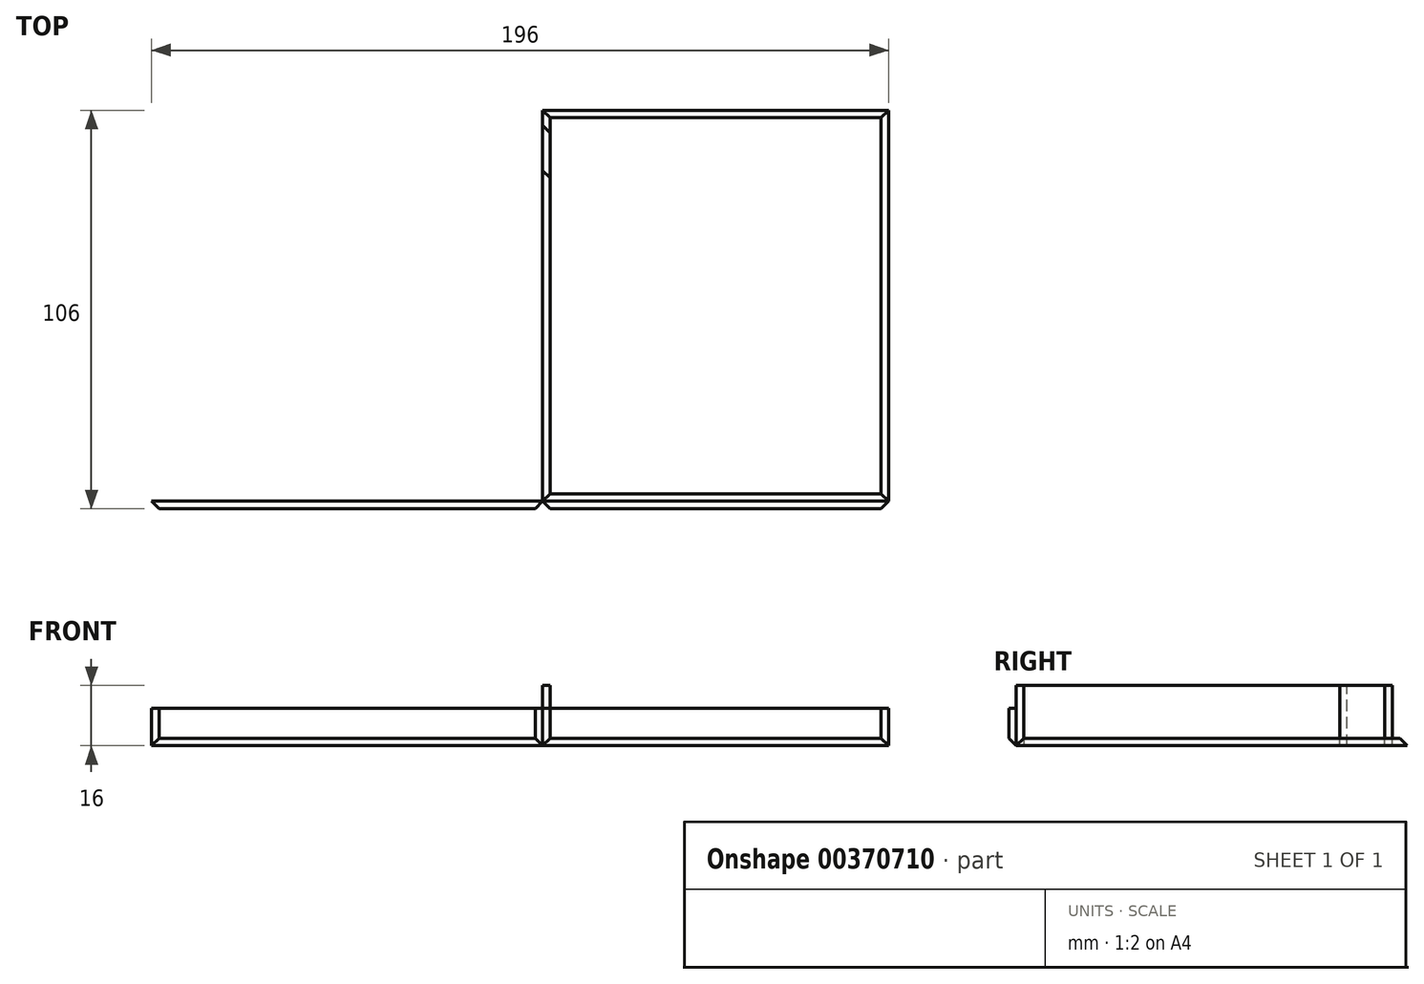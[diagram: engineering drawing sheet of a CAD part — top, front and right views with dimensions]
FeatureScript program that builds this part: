
annotation { "Feature Type Name" : "Feature", "Feature Type Description" : "" }
export const myFeature = defineFeature(function(context is Context, id is Id, definition is map)
    precondition{}
    {
        {
            var Q0;
            Q0=qCreatedBy(makeId("Top.planeOp"),FACE);
            var sketch = newSketch(context, id + "F0", { "sketchPlane" : qUnion([Q0])});
            skLineSegment(sketch, "E0.bottom", {"start": v(0, 0) * mm, "end": v(92, 0) * mm});
            skLineSegment(sketch, "E0.top", {"start": v(0, 104) * mm, "end": v(92, 104) * mm});
            skLineSegment(sketch, "E0.left", {"start": v(0, 0) * mm, "end": v(0, 104) * mm});
            skLineSegment(sketch, "E0.right", {"start": v(92, 0) * mm, "end": v(92, 104) * mm});
            skSolve(sketch);
        }
        {
            var Q0;
            Q0=makeQuery(id+"F0.imprint","IMPRINT",FACE,{"disambiguationData":[TD([[makeQuery(id+"F0.imprint","IMPRINT",EDGE,{"derivedFrom":sQuery(id+"F0.wireOp",EDGE,"E0.bottom")}),1.0]])]});
            extrude(context, id + "F1", {"entities" : qUnion([Q0]), "depth" : 2 * mm});
        }
        {
            var Q0;
            Q0=makeQuery(id+"F1.opExtrude","CAP_FACE",FACE,{"disambiguationData":[OSD([sQuery(id+"F0.wireOp",EDGE,"E0.bottom"),sQuery(id+"F0.wireOp",EDGE,"E0.top"),sQuery(id+"F0.wireOp",EDGE,"E0.left"),sQuery(id+"F0.wireOp",EDGE,"E0.right")])],"isStart":false});
            chamfer(context, id + "F2", {"entities" : qUnion([Q0]), "width" : 2 * mm, "tangentPropagation" : true});
        }
        {
            var Q0;
            Q0=qCreatedBy(makeId("Front.planeOp"),FACE);
            var sketch = newSketch(context, id + "F3", { "sketchPlane" : qUnion([Q0])});
            skLineSegment(sketch, "E1.bottom", {"start": v(0, 0) * mm, "end": v(-104, 0) * mm});
            skLineSegment(sketch, "E1.top", {"start": v(0, 10) * mm, "end": v(-104, 10) * mm});
            skLineSegment(sketch, "E1.left", {"start": v(0, 0) * mm, "end": v(0, 10) * mm});
            skLineSegment(sketch, "E1.right", {"start": v(-104, 0) * mm, "end": v(-104, 10) * mm});
            skSolve(sketch);
        }
        {
            var Q0;
            Q0=makeQuery(id+"F3.imprint","IMPRINT",FACE,{"disambiguationData":[TD([[makeQuery(id+"F3.imprint","IMPRINT",EDGE,{"derivedFrom":sQuery(id+"F3.wireOp",EDGE,"E1.bottom")}),-1.0]])]});
            extrude(context, id + "F4", {"entities" : qUnion([Q0]), "depth" : 2 * mm});
        }
        {
            var Q0;
            Q0=makeQuery(id+"F4.opExtrude","CAP_EDGE",EDGE,{"disambiguationData":[OSD([sQuery(id+"F3.wireOp",EDGE,"E1.bottom")])],"isStart":false});
            var Q1;
            Q1=makeQuery(id+"F4.opExtrude","CAP_EDGE",EDGE,{"disambiguationData":[OSD([sQuery(id+"F3.wireOp",EDGE,"E1.left")])],"isStart":false});
            var Q2;
            Q2=makeQuery(id+"F4.opExtrude","CAP_EDGE",EDGE,{"disambiguationData":[OSD([sQuery(id+"F3.wireOp",EDGE,"E1.right")])],"isStart":false});
            chamfer(context, id + "F5", {"entities" : qUnion([Q0, Q1, Q2]), "width" : 2 * mm, "tangentPropagation" : true});
        }
        {
            var Q0;
            Q0=qCreatedBy(makeId("Front.planeOp"),FACE);
            var sketch = newSketch(context, id + "F6", { "sketchPlane" : qUnion([Q0])});
            skLineSegment(sketch, "E2.bottom", {"start": v(0, 0) * mm, "end": v(92, 0) * mm});
            skLineSegment(sketch, "E2.top", {"start": v(0, 10) * mm, "end": v(92, 10) * mm});
            skLineSegment(sketch, "E2.left", {"start": v(0, 0) * mm, "end": v(0, 10) * mm});
            skLineSegment(sketch, "E2.right", {"start": v(92, 0) * mm, "end": v(92, 10) * mm});
            skSolve(sketch);
        }
        {
            var Q0;
            Q0=makeQuery(id+"F6.imprint","IMPRINT",FACE,{"disambiguationData":[TD([[makeQuery(id+"F6.imprint","IMPRINT",EDGE,{"derivedFrom":sQuery(id+"F6.wireOp",EDGE,"E2.bottom")}),1.0]])]});
            extrude(context, id + "F7", {"entities" : qUnion([Q0]), "depth" : 2 * mm});
        }
        {
            var Q0;
            Q0=makeQuery(id+"F7.opExtrude","CAP_EDGE",EDGE,{"disambiguationData":[OSD([sQuery(id+"F6.wireOp",EDGE,"E2.left")])],"isStart":false});
            var Q1;
            Q1=makeQuery(id+"F7.opExtrude","CAP_EDGE",EDGE,{"disambiguationData":[OSD([sQuery(id+"F6.wireOp",EDGE,"E2.bottom")])],"isStart":false});
            var Q2;
            Q2=makeQuery(id+"F7.opExtrude","CAP_EDGE",EDGE,{"disambiguationData":[OSD([sQuery(id+"F6.wireOp",EDGE,"E2.right")])],"isStart":false});
            chamfer(context, id + "F8", {"entities" : qUnion([Q0, Q1, Q2]), "width" : 2 * mm, "tangentPropagation" : true});
        }
        {
            var Q0;
            Q0=qCreatedBy(makeId("Right.planeOp"),FACE);
            var sketch = newSketch(context, id + "F9", { "sketchPlane" : qUnion([Q0])});
            skLineSegment(sketch, "E3.bottom", {"start": v(0, 0) * mm, "end": v(100, 0) * mm});
            skLineSegment(sketch, "E3.top", {"start": v(0, 16) * mm, "end": v(100, 16) * mm});
            skLineSegment(sketch, "E3.left", {"start": v(0, 0) * mm, "end": v(0, 16) * mm});
            skLineSegment(sketch, "E3.right", {"start": v(100, 0) * mm, "end": v(100, 16) * mm});
            skSolve(sketch);
        }
        {
            var Q0;
            Q0=makeQuery(id+"F9.imprint","IMPRINT",FACE,{"disambiguationData":[TD([[makeQuery(id+"F9.imprint","IMPRINT",EDGE,{"derivedFrom":sQuery(id+"F9.wireOp",EDGE,"E3.bottom")}),1.0]])]});
            extrude(context, id + "F10", {"entities" : qUnion([Q0]), "depth" : 2 * mm});
        }
        {
            var Q0;
            Q0=makeQuery(id+"F10.opExtrude","CAP_EDGE",EDGE,{"disambiguationData":[OSD([sQuery(id+"F9.wireOp",EDGE,"E3.right")])],"isStart":false});
            var Q1;
            Q1=makeQuery(id+"F10.opExtrude","CAP_EDGE",EDGE,{"disambiguationData":[OSD([sQuery(id+"F9.wireOp",EDGE,"E3.left")])],"isStart":false});
            chamfer(context, id + "F11", {"entities" : qUnion([Q0, Q1]), "width" : 2 * mm, "tangentPropagation" : true});
        }
        {
            var Q0;
            Q0=qCreatedBy(makeId("Right.planeOp"),FACE);
            var sketch = newSketch(context, id + "F12", { "sketchPlane" : qUnion([Q0])});
            skLineSegment(sketch, "E4.bottom", {"start": v(0, 0) * mm, "end": v(88, 0) * mm});
            skLineSegment(sketch, "E4.top", {"start": v(0, 16) * mm, "end": v(88, 16) * mm});
            skLineSegment(sketch, "E4.left", {"start": v(0, 0) * mm, "end": v(0, 16) * mm});
            skLineSegment(sketch, "E4.right", {"start": v(88, 0) * mm, "end": v(88, 16) * mm});
            skSolve(sketch);
        }
        {
            var Q0;
            Q0=makeQuery(id+"F12.imprint","IMPRINT",FACE,{"disambiguationData":[TD([[makeQuery(id+"F12.imprint","IMPRINT",EDGE,{"derivedFrom":sQuery(id+"F12.wireOp",EDGE,"E4.bottom")}),1.0]])]});
            extrude(context, id + "F13", {"entities" : qUnion([Q0]), "depth" : 2 * mm});
        }
        {
            var Q0;
            Q0=makeQuery(id+"F13.opExtrude","CAP_EDGE",EDGE,{"disambiguationData":[OSD([sQuery(id+"F12.wireOp",EDGE,"E4.left")])],"isStart":false});
            var Q1;
            Q1=makeQuery(id+"F13.opExtrude","CAP_EDGE",EDGE,{"disambiguationData":[OSD([sQuery(id+"F12.wireOp",EDGE,"E4.right")])],"isStart":false});
            chamfer(context, id + "F14", {"entities" : qUnion([Q0, Q1]), "width" : 2 * mm, "tangentPropagation" : true});
        }
    });
